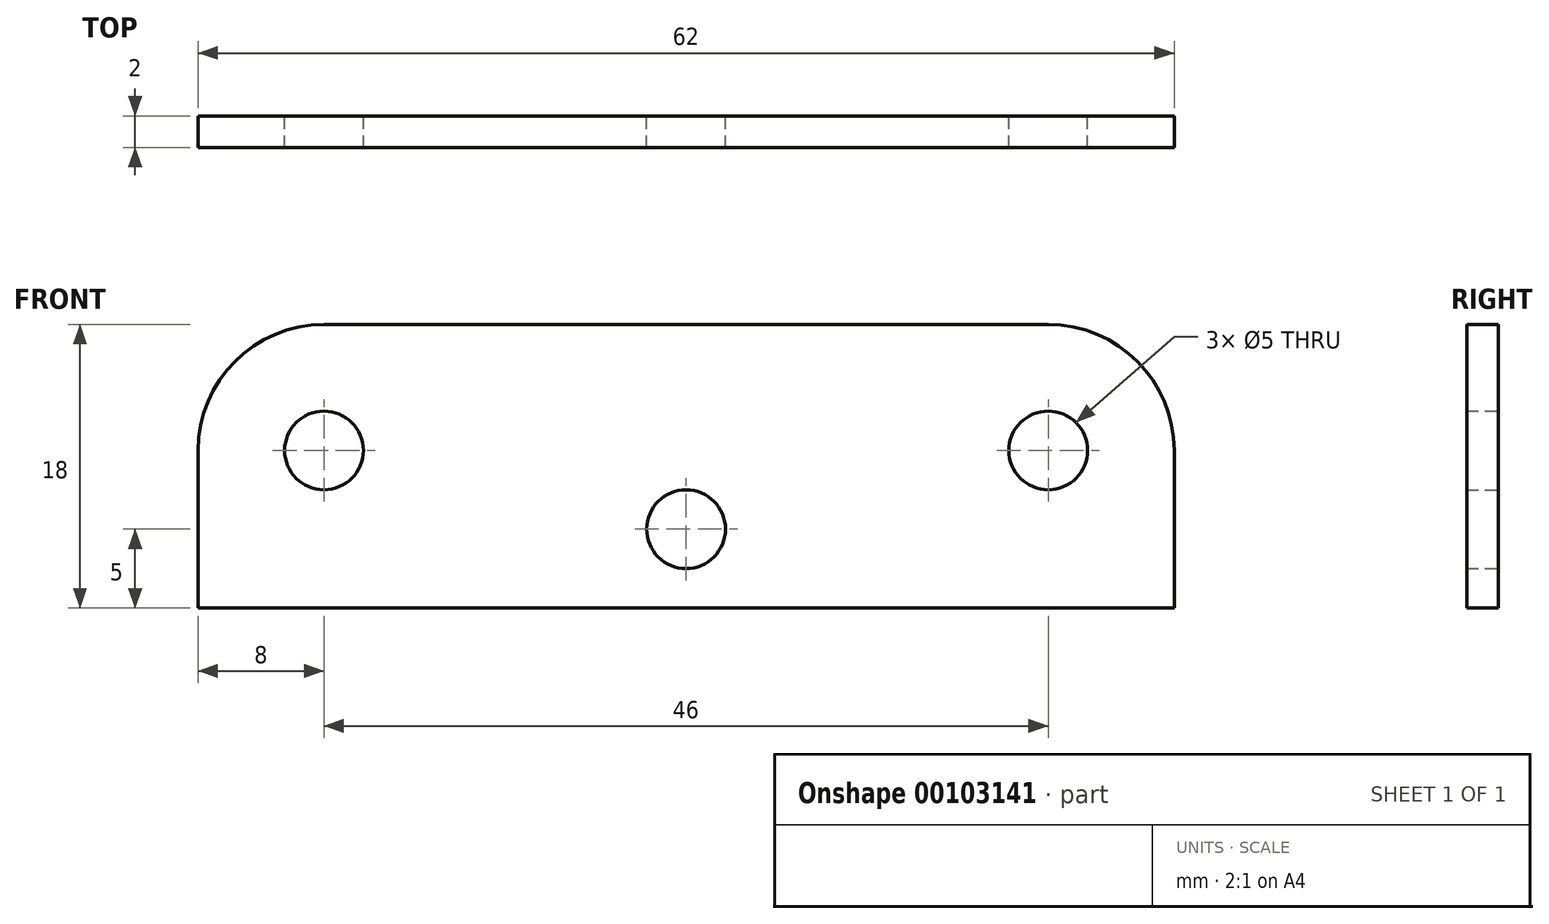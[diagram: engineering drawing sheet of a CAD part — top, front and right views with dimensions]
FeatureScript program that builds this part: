
annotation { "Feature Type Name" : "Feature", "Feature Type Description" : "" }
export const myFeature = defineFeature(function(context is Context, id is Id, definition is map)
    precondition{}
    {
        {
            var Q0;
            Q0=qCreatedBy(makeId("Front.planeOp"),FACE);
            var sketch = newSketch(context, id + "F0", { "sketchPlane" : qUnion([Q0])});
            skLineSegment(sketch, "E0.bottom", {"start": v(31, -9) * mm, "end": v(-31, -9) * mm});
            skLineSegment(sketch, "E0.top", {"start": v(23, 9) * mm, "end": v(-23, 9) * mm});
            skLineSegment(sketch, "E0.left", {"start": v(31, -9) * mm, "end": v(31, 1) * mm});
            skLineSegment(sketch, "E0.right", {"start": v(-31, -9) * mm, "end": v(-31, 1) * mm});
            skPoint(sketch, "E0.middle", {"position": v(0, 0) * mm});
            skPoint(sketch, "E1.visualSharp", {"position": v(-31, 9) * mm});
            skArc(sketch, "E1.filletArc", {"start": v(-23, 9) * mm, "mid": v(-28.66, 6.66) * mm, "end": v(-31, 1) * mm});
            skPoint(sketch, "E2.visualSharp", {"position": v(31, 9) * mm});
            skArc(sketch, "E2.filletArc", {"start": v(31, 1) * mm, "mid": v(28.66, 6.66) * mm, "end": v(23, 9) * mm});
            skCircle(sketch, "E3", {"center": v(0, -4) * mm, "radius": 2.5 * mm});
            skCircle(sketch, "E4", {"center": v(23, 1) * mm, "radius": 2.5 * mm});
            skCircle(sketch, "E5", {"center": v(-23, 1) * mm, "radius": 2.5 * mm});
            skSolve(sketch);
        }
        {
            var Q0;
            Q0=makeQuery(id+"F0.imprint","IMPRINT",FACE,{"disambiguationData":[TD([[makeQuery(id+"F0.imprint","IMPRINT",EDGE,{"derivedFrom":sQuery(id+"F0.wireOp",EDGE,"E0.bottom")}),-1.0]])]});
            extrude(context, id + "F1", {"entities" : qUnion([Q0]), "flatOperationType" : FlatOperationType.REMOVE, "depth" : 2 * mm, "offsetDistance" : 25 * mm, "domain" : OperationDomain.MODEL});
        }
    });
